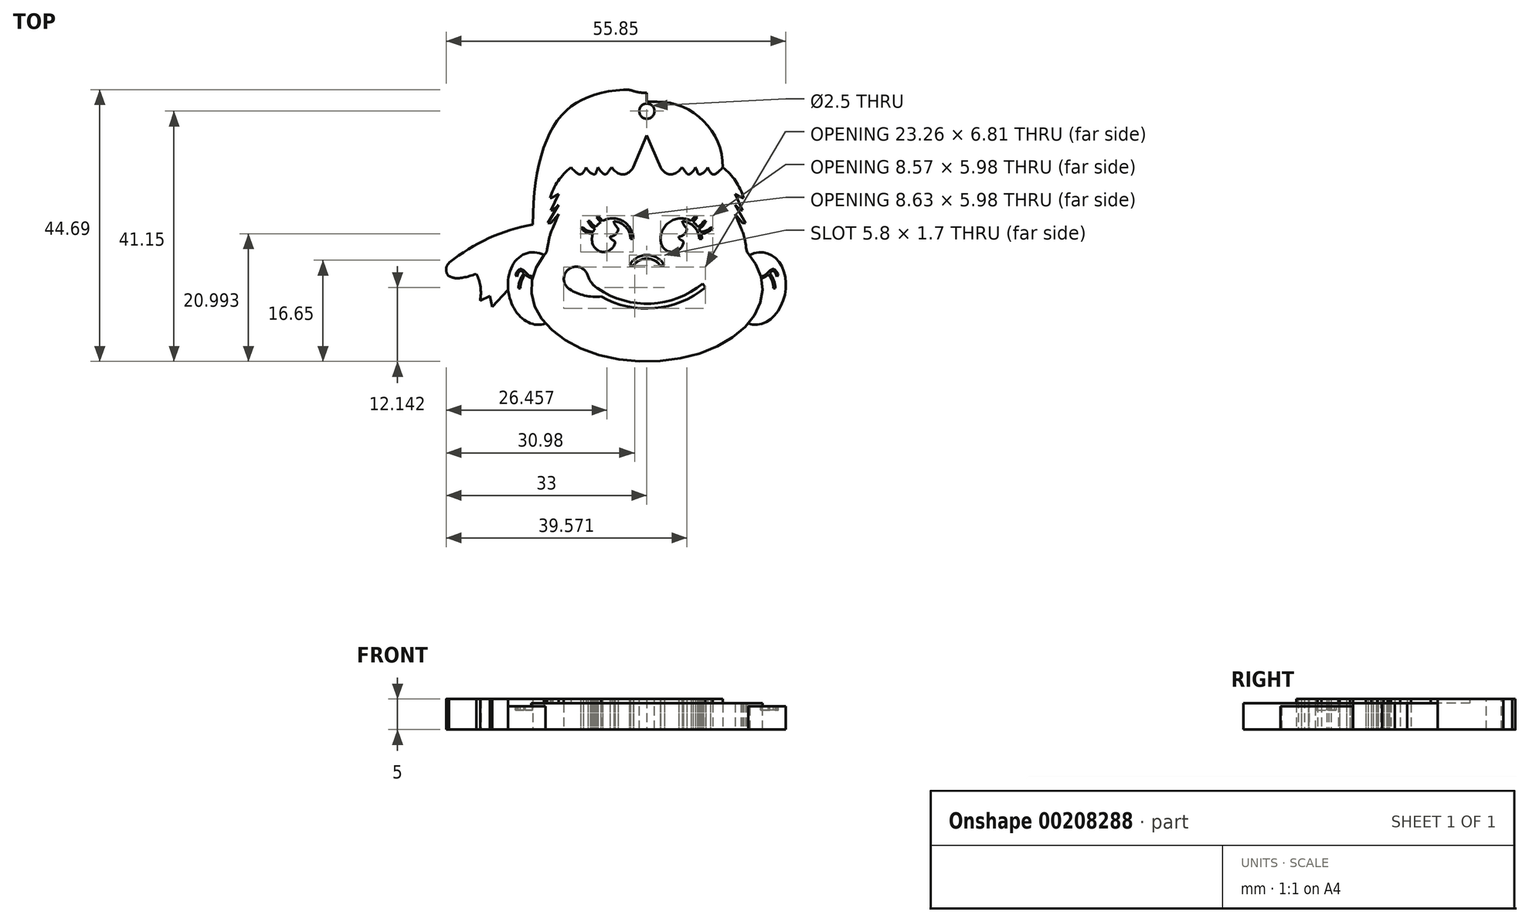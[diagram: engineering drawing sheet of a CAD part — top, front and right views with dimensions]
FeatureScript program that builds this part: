
annotation { "Feature Type Name" : "Feature", "Feature Type Description" : "" }
export const myFeature = defineFeature(function(context is Context, id is Id, definition is map)
    precondition{}
    {
        {
            var Q0;
            Q0=qCreatedBy(makeId("Top.planeOp"),FACE);
            var sketch = newSketch(context, id + "F0", { "sketchPlane" : qUnion([Q0])});
            skEllipticalArc(sketch, "E0", {});
            skLineSegment(sketch, "E1", {"start": v(-16.45, 0) * mm, "end": v(16.45, 0) * mm, "construction": true});
            skLineSegment(sketch, "E2", {"start": v(-35.38, -6) * mm, "end": v(38.73, -6) * mm, "construction": true});
            skPoint(sketch, "E2.endSnap0", {"position": v(19, -6) * mm});
            skLineSegment(sketch, "E3", {"start": v(-21.52, 12.24) * mm, "end": v(-13.55, -32.91) * mm, "construction": true});
            skEllipticalArc(sketch, "E4", {});
            skLineSegment(sketch, "E5", {"start": v(-19.34, -0.1) * mm, "end": v(-17.26, -11.9) * mm, "construction": true});
            skLineSegment(sketch, "E6", {"start": v(0, 48.23) * mm, "end": v(0, -36.68) * mm, "construction": true});
            skArc(sketch, "E7", {"start": v(2.9, -2.2) * mm, "mid": v(0, -0.5) * mm, "end": v(-2.9, -2.2) * mm});
            skLineSegment(sketch, "E8", {"start": v(-2.28, -0.5) * mm, "end": v(3.74, -0.5) * mm, "construction": true});
            skFitSpline(sketch, "E9", {"points": [v(-16.45, 0) * mm, v(-16, 2.5) * mm, v(-14.5, 6.25) * mm], "startDerivative": vector(1.72, 10.17) * mm, "endDerivative": vector(6.18, 14.8) * mm});
            skLineSegment(sketch, "E10", {"start": v(-16.25, 4.75) * mm, "end": v(-14.5, 7.75) * mm});
            skLineSegment(sketch, "E11", {"start": v(-14.5, 7.75) * mm, "end": v(-15.45, 6.85) * mm});
            skLineSegment(sketch, "E12", {"start": v(-15.45, 6.85) * mm, "end": v(-15.75, 6.85) * mm});
            skLineSegment(sketch, "E13", {"start": v(-15.75, 6.85) * mm, "end": v(-14.5, 9.5) * mm});
            skLineSegment(sketch, "E14", {"start": v(-16.25, 4.75) * mm, "end": v(-15.75, 4.75) * mm});
            skLineSegment(sketch, "E15", {"start": v(-15.75, 4.75) * mm, "end": v(-14.5, 6.25) * mm});
            skLineSegment(sketch, "E16", {"start": v(-14.5, 9.5) * mm, "end": v(-15.7, 8.9) * mm});
            skLineSegment(sketch, "E17", {"start": v(-15.7, 8.9) * mm, "end": v(-15.9, 8.9) * mm});
            skArc(sketch, "E18", {"start": v(-12.5, 13.9) * mm, "mid": v(-14.59, 11.66) * mm, "end": v(-15.9, 8.9) * mm});
            skEllipticalArc(sketch, "E19.trimOffspring", {});
            skLineSegment(sketch, "E20", {"start": v(-12.5, 13.9) * mm, "end": v(0, 13.9) * mm, "construction": true});
            skArc(sketch, "E21.MirrorCS", {"start": v(12.5, 13.9) * mm, "mid": v(14.59, 11.66) * mm, "end": v(15.9, 8.9) * mm});
            skLineSegment(sketch, "E22.MirrorCS", {"start": v(15.7, 8.9) * mm, "end": v(15.9, 8.9) * mm});
            skLineSegment(sketch, "E23.MirrorCS", {"start": v(14.5, 9.5) * mm, "end": v(15.7, 8.9) * mm});
            skLineSegment(sketch, "E24.MirrorCS", {"start": v(12.5, 13.9) * mm, "end": v(0, 13.9) * mm, "construction": true});
            skLineSegment(sketch, "E25.MirrorCS", {"start": v(15.75, 6.85) * mm, "end": v(14.5, 9.5) * mm});
            skLineSegment(sketch, "E26.MirrorCS", {"start": v(15.45, 6.85) * mm, "end": v(15.75, 6.85) * mm});
            skLineSegment(sketch, "E27.MirrorCS", {"start": v(14.5, 7.75) * mm, "end": v(15.45, 6.85) * mm});
            skLineSegment(sketch, "E28.MirrorCS", {"start": v(16.25, 4.75) * mm, "end": v(14.5, 7.75) * mm});
            skLineSegment(sketch, "E29.MirrorCS", {"start": v(16.25, 4.75) * mm, "end": v(15.75, 4.75) * mm});
            skLineSegment(sketch, "E30.MirrorCS", {"start": v(15.75, 4.75) * mm, "end": v(14.5, 6.25) * mm});
            skFitSpline(sketch, "E31.MirrorCS", {"points": [v(16.45, 0) * mm, v(16, 2.5) * mm, v(14.5, 6.25) * mm], "startDerivative": vector(-1.72, 10.17) * mm, "endDerivative": vector(-6.18, 14.8) * mm});
            skEllipticalArc(sketch, "E32.trimOffspring", {});
            skLineSegment(sketch, "E33", {"start": v(-2.9, -2.2) * mm, "end": v(-2.2, -2.2) * mm});
            skLineSegment(sketch, "E34", {"start": v(2.9, -2.2) * mm, "end": v(2.2, -2.2) * mm});
            skLineSegment(sketch, "E35", {"start": v(0, 19.2) * mm, "end": v(-2.25, 13.9) * mm});
            skEllipticalArc(sketch, "E36.MirrorCS", {});
            skLineSegment(sketch, "E37.MirrorCS", {"start": v(21.52, 12.24) * mm, "end": v(13.55, -32.91) * mm, "construction": true});
            skLineSegment(sketch, "E38", {"start": v(0, 24.7) * mm, "end": v(-1.7, 24.7) * mm});
            skArc(sketch, "E39", {"start": v(-1.7, 24.7) * mm, "mid": v(-9.34, 21.54) * mm, "end": v(-12.5, 13.9) * mm});
            skFitSpline(sketch, "E40", {"points": [v(0, 24.7) * mm, v(-8.6, 19.92) * mm, v(-10, 13.9) * mm], "startDerivative": vector(-29.01, -7.2) * mm, "endDerivative": vector(7.13, -17.68) * mm});
            skLineSegment(sketch, "E41", {"start": v(0, 13.9) * mm, "end": v(-8.6, 19.92) * mm, "construction": true});
            skLineSegment(sketch, "E42", {"start": v(-2.25, 13.9) * mm, "end": v(-2.25, 12.75) * mm, "construction": true});
            skLineSegment(sketch, "E43", {"start": v(-2.25, 12.75) * mm, "end": v(-5.75, 12.75) * mm, "construction": true});
            skLineSegment(sketch, "E44", {"start": v(-5.75, 12.75) * mm, "end": v(-5.75, 13.9) * mm, "construction": true});
            skFitSpline(sketch, "E45", {"points": [v(0, 22.2) * mm, v(-6.25, 15.4) * mm, v(-3.95, 12.75) * mm, v(-2.25, 13.9) * mm], "startDerivative": vector(-21.83, -9.77) * mm, "endDerivative": vector(2.48, 5.84) * mm});
            skLineSegment(sketch, "E46", {"start": v(-5.75, 12.75) * mm, "end": v(-22.47, 12.75) * mm, "construction": true});
            skFitSpline(sketch, "E47", {"points": [v(-10, 13.9) * mm, v(-8.7, 12.75) * mm, v(-8, 13.9) * mm], "startDerivative": vector(1.16, -2.87) * mm, "endDerivative": vector(1.96, 4.18) * mm});
            skLineSegment(sketch, "E48", {"start": v(0, 23.3) * mm, "end": v(20, 23.3) * mm, "construction": true});
            skLineSegment(sketch, "E49", {"start": v(-8.6, 16.55) * mm, "end": v(-9.48, 16.55) * mm, "construction": true});
            skFitSpline(sketch, "E50", {"points": [v(0, 23.3) * mm, v(-8.6, 16.55) * mm, v(-6.85, 12.75) * mm, v(-5.75, 13.9) * mm], "startDerivative": vector(-25.25, -9.56) * mm, "endDerivative": vector(8.03, 6.02) * mm});
            skFitSpline(sketch, "E51", {"points": [v(-12.5, 13.9) * mm, v(-10.9, 12.75) * mm, v(-10, 13.9) * mm], "startDerivative": vector(3.54, -3.37) * mm, "endDerivative": vector(1.39, 3.6) * mm});
            skLineSegment(sketch, "E52", {"start": v(0, 24.7) * mm, "end": v(0, 19.2) * mm});
            skFitSpline(sketch, "E53.MirrorCS", {"points": [v(12.5, 13.9) * mm, v(10.9, 12.75) * mm, v(10, 13.9) * mm], "startDerivative": vector(-3.54, -3.37) * mm, "endDerivative": vector(-1.39, 3.6) * mm});
            skFitSpline(sketch, "E54.MirrorCS", {"points": [v(10, 13.9) * mm, v(8.7, 12.75) * mm, v(8, 13.9) * mm], "startDerivative": vector(-1.16, -2.87) * mm, "endDerivative": vector(-1.96, 4.18) * mm});
            skFitSpline(sketch, "E55.MirrorCS", {"points": [v(0, 23.3) * mm, v(8.6, 16.55) * mm, v(6.85, 12.75) * mm, v(5.75, 13.9) * mm], "startDerivative": vector(25.25, -9.56) * mm, "endDerivative": vector(-8.03, 6.02) * mm});
            skFitSpline(sketch, "E56.MirrorCS", {"points": [v(0, 22.2) * mm, v(6.25, 15.4) * mm, v(3.95, 12.75) * mm, v(2.25, 13.9) * mm], "startDerivative": vector(21.83, -9.77) * mm, "endDerivative": vector(-2.48, 5.84) * mm});
            skLineSegment(sketch, "E57.MirrorCS", {"start": v(0, 19.2) * mm, "end": v(2.25, 13.9) * mm});
            skFitSpline(sketch, "E58.MirrorCS", {"points": [v(0, 24.7) * mm, v(8.6, 19.92) * mm, v(10, 13.9) * mm], "startDerivative": vector(29.01, -7.2) * mm, "endDerivative": vector(-7.13, -17.68) * mm});
            skArc(sketch, "E59.MirrorCS", {"start": v(1.7, 24.7) * mm, "mid": v(9.34, 21.54) * mm, "end": v(12.5, 13.9) * mm});
            skLineSegment(sketch, "E60.MirrorCS", {"start": v(0, 24.7) * mm, "end": v(1.7, 24.7) * mm});
            skEllipticalArc(sketch, "E61", {});
            skEllipticalArc(sketch, "E62.trimOffspring", {});
            skArc(sketch, "E63", {"start": v(-8.98, 1.61) * mm, "mid": v(-7.2, 0) * mm, "end": v(-5.26, 1.43) * mm});
            skArc(sketch, "E64", {"start": v(-2.25, 2.5) * mm, "mid": v(-4.06, 5.14) * mm, "end": v(-7.26, 5.1) * mm});
            skLineSegment(sketch, "E65", {"start": v(-5.5, 5.5) * mm, "end": v(-5.5, -1.83) * mm, "construction": true});
            skArc(sketch, "E66", {"start": v(-5.45, 5.07) * mm, "mid": v(-5.23, 4.5) * mm, "end": v(-4.85, 4.02) * mm});
            skArc(sketch, "E67", {"start": v(-6.04, 2.51) * mm, "mid": v(-5.88, 2.14) * mm, "end": v(-5.54, 1.91) * mm});
            skArc(sketch, "E68", {"start": v(-6.04, 2.51) * mm, "mid": v(-5.18, 2.85) * mm, "end": v(-4.72, 3.65) * mm});
            skPoint(sketch, "E69.visualSharp", {"position": v(-4.7, 3.9) * mm});
            skArc(sketch, "E69.filletArc", {"start": v(-4.72, 3.65) * mm, "mid": v(-4.74, 3.85) * mm, "end": v(-4.85, 4.02) * mm});
            skPoint(sketch, "E70.visualSharp", {"position": v(-5.2, 1.9) * mm});
            skArc(sketch, "E70.filletArc", {"start": v(-5.26, 1.43) * mm, "mid": v(-5.3, 1.73) * mm, "end": v(-5.54, 1.91) * mm});
            skPoint(sketch, "E71.start.orphan", {"position": v(-8.75, 2.5) * mm});
            skLineSegment(sketch, "E72", {"start": v(-7.26, 5.1) * mm, "end": v(-8, 5.98) * mm});
            skLineSegment(sketch, "E73", {"start": v(-8, 5.98) * mm, "end": v(-8.3, 5.73) * mm});
            skLineSegment(sketch, "E74", {"start": v(-8.3, 5.73) * mm, "end": v(-7.6, 4.89) * mm});
            skArc(sketch, "E75.trimOffspring", {"start": v(-7.6, 4.89) * mm, "mid": v(-8.01, 4.54) * mm, "end": v(-8.36, 4.14) * mm});
            skArc(sketch, "E76", {"start": v(-9.3, 5.05) * mm, "mid": v(-8.91, 4.51) * mm, "end": v(-8.36, 4.14) * mm});
            skArc(sketch, "E77", {"start": v(-9.7, 5.05) * mm, "mid": v(-9.25, 4.34) * mm, "end": v(-8.56, 3.83) * mm});
            skLineSegment(sketch, "E78", {"start": v(-9.7, 5.05) * mm, "end": v(-9.3, 5.05) * mm});
            skArc(sketch, "E79.trimOffspring", {"start": v(-8.56, 3.83) * mm, "mid": v(-8.7, 3.58) * mm, "end": v(-8.8, 3.33) * mm});
            skArc(sketch, "E80", {"start": v(-10.46, 4) * mm, "mid": v(-9.7, 3.47) * mm, "end": v(-8.8, 3.33) * mm});
            skLineSegment(sketch, "E81", {"start": v(-10.46, 4) * mm, "end": v(-10.86, 4) * mm});
            skArc(sketch, "E82", {"start": v(-10.86, 4) * mm, "mid": v(-10, 3.26) * mm, "end": v(-8.9, 3) * mm});
            skArc(sketch, "E83.trimOffspring", {"start": v(-8.9, 3) * mm, "mid": v(-9.02, 2.31) * mm, "end": v(-8.98, 1.61) * mm});
            skLineSegment(sketch, "E84", {"start": v(0, 54) * mm, "end": v(50, 54) * mm, "construction": true});
            skLineSegment(sketch, "E85", {"start": v(50, 54) * mm, "end": v(50, -14.33) * mm, "construction": true});
            skLineSegment(sketch, "E86", {"start": v(55.52, 54) * mm, "end": v(55.52, -14.1) * mm, "construction": true});
            skArc(sketch, "E87", {"start": v(-8.1, -6) * mm, "mid": v(0, -8.5) * mm, "end": v(8.1, -6) * mm, "construction": true});
            skArc(sketch, "E88", {"start": v(-8.1, -6) * mm, "mid": v(0.67, -8.48) * mm, "end": v(9.16, -5.2) * mm});
            skLineSegment(sketch, "E89", {"start": v(9.16, -5.2) * mm, "end": v(9.61, -5.86) * mm});
            skLineSegment(sketch, "E90", {"start": v(-10.95, -7.1) * mm, "end": v(9.68, -7.1) * mm, "construction": true});
            skArc(sketch, "E91", {"start": v(-9.75, -3.8) * mm, "mid": v(-9.1, -5.04) * mm, "end": v(-8.1, -6) * mm});
            skArc(sketch, "E92", {"start": v(-9.75, -3.8) * mm, "mid": v(-12.88, -2.84) * mm, "end": v(-12.73, -6.1) * mm});
            skArc(sketch, "E93", {"start": v(-12.73, -6.1) * mm, "mid": v(-10.22, -7.16) * mm, "end": v(-7.5, -7.31) * mm});
            skArc(sketch, "E94", {"start": v(-7.5, -7.31) * mm, "mid": v(1.28, -9.24) * mm, "end": v(9.61, -5.86) * mm});
            skArc(sketch, "E95", {"start": v(-2.23, 2.13) * mm, "mid": v(-2.23, 2.31) * mm, "end": v(-2.25, 2.5) * mm});
            skLineSegment(sketch, "E96", {"start": v(-2.68, 2.13) * mm, "end": v(-2.23, 2.13) * mm});
            skArc(sketch, "E97", {"start": v(2.2, -2.2) * mm, "mid": v(0, -1.09) * mm, "end": v(-2.2, -2.2) * mm});
            skLineSegment(sketch, "E98", {"start": v(-18.75, 27.8) * mm, "end": v(-18.75, -30.49) * mm, "construction": true});
            skLineSegment(sketch, "E99", {"start": v(-15.9, 26.75) * mm, "end": v(30.98, 26.75) * mm, "construction": true});
            skLineSegment(sketch, "E100", {"start": v(-34.8, 4.5) * mm, "end": v(31.88, 4.5) * mm, "construction": true});
            skFitSpline(sketch, "E101", {"points": [v(-18.75, 4.5) * mm, v(-13.75, 22.75) * mm, v(-2.5, 26.75) * mm], "startDerivative": vector(0, 44.41) * mm, "endDerivative": vector(32.74, 1.2) * mm});
            skEllipticalArc(sketch, "E102", {});
            skArc(sketch, "E103.filletArc", {"start": v(-2.11, 26.43) * mm, "mid": v(-2.95, 26.65) * mm, "end": v(-3.82, 26.68) * mm});
            skLineSegment(sketch, "E104", {"start": v(-33, 13.01) * mm, "end": v(-33, -15.44) * mm, "construction": true});
            skLineSegment(sketch, "E105", {"start": v(-45.55, -3.5) * mm, "end": v(13.92, -3.5) * mm, "construction": true});
            skArc(sketch, "E106", {"start": v(-18.75, 4.5) * mm, "mid": v(-26, 2.25) * mm, "end": v(-32.44, -1.74) * mm});
            skArc(sketch, "E107", {"start": v(-32.44, -1.74) * mm, "mid": v(-33, -2.84) * mm, "end": v(-32.55, -3.98) * mm});
            skArc(sketch, "E108", {"start": v(-27.41, -8) * mm, "mid": v(-27.35, -5.76) * mm, "end": v(-28.02, -3.62) * mm});
            skLineSegment(sketch, "E109", {"start": v(-27.41, -8) * mm, "end": v(-25.81, -7.21) * mm});
            skLineSegment(sketch, "E110", {"start": v(-25.81, -7.21) * mm, "end": v(-25.41, -9) * mm});
            skLineSegment(sketch, "E111", {"start": v(-25.41, -9) * mm, "end": v(-22.81, -6.2) * mm});
            skFitSpline(sketch, "E112", {"points": [v(-32.55, -3.98) * mm, v(-30.97, -4.3) * mm, v(-24.48, -2.33) * mm], "startDerivative": vector(4.01, -1.65) * mm, "endDerivative": vector(11.28, 4.26) * mm});
            skPoint(sketch, "E113.orphan", {"position": v(-28.21, -3.27) * mm});
            skLineSegment(sketch, "E114", {"start": v(0, 26.15) * mm, "end": v(0, 24.7) * mm});
            skArc(sketch, "E115.1.0.0", {"start": v(2.38, 3) * mm, "mid": v(2.26, 2.31) * mm, "end": v(2.3, 1.61) * mm});
            skArc(sketch, "E115.1.0.1", {"start": v(2.3, 1.61) * mm, "mid": v(4.09, 0) * mm, "end": v(6.02, 1.43) * mm});
            skArc(sketch, "E115.1.0.2", {"start": v(6.02, 1.43) * mm, "mid": v(5.98, 1.73) * mm, "end": v(5.74, 1.91) * mm});
            skArc(sketch, "E115.1.0.3", {"start": v(5.24, 2.51) * mm, "mid": v(5.4, 2.14) * mm, "end": v(5.74, 1.91) * mm});
            skArc(sketch, "E115.1.0.4", {"start": v(5.24, 2.51) * mm, "mid": v(6.1, 2.85) * mm, "end": v(6.56, 3.65) * mm});
            skArc(sketch, "E115.1.0.5", {"start": v(6.56, 3.65) * mm, "mid": v(6.54, 3.85) * mm, "end": v(6.43, 4.02) * mm});
            skArc(sketch, "E115.1.0.6", {"start": v(5.83, 5.07) * mm, "mid": v(6.05, 4.5) * mm, "end": v(6.43, 4.02) * mm});
            skLineSegment(sketch, "E115.1.0.9", {"start": v(8.6, 2.13) * mm, "end": v(9.05, 2.13) * mm});
            skLineSegment(sketch, "E115.direction1", {"start": v(-8.98, 1.61) * mm, "end": v(2.3, 1.61) * mm, "construction": true});
            skArc(sketch, "E116", {"start": v(9.05, 2.13) * mm, "mid": v(9.02, 2.57) * mm, "end": v(8.93, 3) * mm});
            skArc(sketch, "E117.MirrorCS", {"start": v(10.86, 4) * mm, "mid": v(10.02, 3.27) * mm, "end": v(8.93, 3) * mm});
            skLineSegment(sketch, "E118.MirrorCS", {"start": v(9.7, 5.05) * mm, "end": v(9.3, 5.05) * mm});
            skArc(sketch, "E119.MirrorCS", {"start": v(9.7, 5.05) * mm, "mid": v(9.25, 4.35) * mm, "end": v(8.59, 3.84) * mm});
            skLineSegment(sketch, "E120.MirrorCS", {"start": v(10.46, 4) * mm, "end": v(10.86, 4) * mm});
            skArc(sketch, "E121.MirrorCS", {"start": v(10.46, 4) * mm, "mid": v(9.72, 3.48) * mm, "end": v(8.83, 3.33) * mm});
            skArc(sketch, "E122.MirrorCS", {"start": v(9.3, 5.05) * mm, "mid": v(8.92, 4.52) * mm, "end": v(8.38, 4.15) * mm});
            skLineSegment(sketch, "E123.MirrorCS", {"start": v(7.27, 5.11) * mm, "end": v(8, 5.98) * mm});
            skLineSegment(sketch, "E124.MirrorCS", {"start": v(8, 5.98) * mm, "end": v(8.3, 5.73) * mm});
            skLineSegment(sketch, "E125.MirrorCS", {"start": v(8.3, 5.73) * mm, "end": v(7.61, 4.9) * mm});
            skPoint(sketch, "E126.orphan", {"position": v(7.26, 5.1) * mm});
            skPoint(sketch, "E127.orphan", {"position": v(7.6, 4.89) * mm});
            skArc(sketch, "E128.trimOffspring", {"start": v(7.27, 5.11) * mm, "mid": v(4.31, 5.25) * mm, "end": v(2.38, 3) * mm});
            skPoint(sketch, "E129.orphan", {"position": v(8.9, 3) * mm});
            skPoint(sketch, "E130.orphan", {"position": v(8.8, 3.33) * mm});
            skArc(sketch, "E131.trimOffspring", {"start": v(8.83, 3.33) * mm, "mid": v(8.72, 3.59) * mm, "end": v(8.59, 3.84) * mm});
            skArc(sketch, "E132.trimOffspring", {"start": v(8.38, 4.15) * mm, "mid": v(8.03, 4.56) * mm, "end": v(7.61, 4.9) * mm});
            skPoint(sketch, "E133.orphan", {"position": v(8.36, 4.14) * mm});
            skPoint(sketch, "E134.orphan", {"position": v(8.56, 3.83) * mm});
            skArc(sketch, "E135", {"start": v(-2.68, 2.13) * mm, "mid": v(-3.48, 4.15) * mm, "end": v(-5.45, 5.07) * mm});
            skPoint(sketch, "E136.orphan", {"position": v(-5.47, 5.17) * mm});
            skArc(sketch, "E137", {"start": v(8.6, 2.13) * mm, "mid": v(7.8, 4.15) * mm, "end": v(5.83, 5.07) * mm});
            skPoint(sketch, "E138.orphan", {"position": v(5.8, 5.17) * mm});
            const initialGuessF0  = {"E0": [0, -0.006, 1, 0, 0.019, 0.012, 2.6179938779914944, 2.668435409031319], "E4": [-0.0183, -0.006, -0.17364817766693047, 0.9848077530122081, 0.006, 0.0045, 5.742579078983642, 3.2755769125221526], "E19.trimOffspring": [0, -0.006, 1, 0, 0.019, 0.012, 3.641440500266903, 5.7833374605024765], "E32.trimOffspring": [0, -0.006, 1, 0, 0.019, 0.012, 0.47315724455847397, 0.5235987755982988], "E36.MirrorCS": [0.0183, -0.006, 0.17364817766693047, 0.9848077530122081, 0.006, 0.0045, 3.0076083946574337, 0.5406062281959443], "E61": [0, -0.006, 1, 0, 0.019, 0.012, 2.6684354090313196, 3.6414405002669024], "E62.trimOffspring": [0, -0.006, 1, 0, 0.019, 0.012, 5.7833374605024765, 0.47315724455847347], "E102": [0, 0.02675, -1, 0, 0.0025, 0.0006, 0.5643852426448737, 1.5707963267948966]};
            skSetInitialGuess(sketch, initialGuessF0);
            skSolve(sketch);
        }
        {
            var Q0;
            Q0=makeQuery(id+"F0.imprint","IMPRINT",FACE,{"disambiguationData":[TD([[makeQuery(id+"F0.imprint","IMPRINT",EDGE,{"derivedFrom":sQuery(id+"F0.wireOp",EDGE,"E0")}),1.0]])]});
            var Q1;
            Q1=makeQuery(id+"F0.imprint","IMPRINT",FACE,{"disambiguationData":[TD([[makeQuery(id+"F0.imprint","IMPRINT",EDGE,{"derivedFrom":sQuery(id+"F0.wireOp",EDGE,"ICi0ZoLA-6eNF-tacr-hD6t-iQozf2GyN9Os")}),1.0]])]});
            var Q2;
            Q2=makeQuery(id+"F0.imprint","IMPRINT",FACE,{"disambiguationData":[TD([[makeQuery(id+"F0.imprint","IMPRINT",EDGE,{"derivedFrom":sQuery(id+"F0.wireOp",EDGE,"Alc9XebQ-BCgD-IBuf-yUf6-nh8GaAThc2JX")}),-1.0]])]});
            var Q3;
            Q3=makeQuery(id+"F0.imprint","IMPRINT",FACE,{"disambiguationData":[TD([[makeQuery(id+"F0.imprint","IMPRINT",EDGE,{"derivedFrom":sQuery(id+"F0.wireOp",EDGE,"39c14105-0e34-43a8-b0d7-4433907fe2a90.MirrorCS")}),1.0]])]});
            extrude(context, id + "F1", {"entities" : qUnion([Q0, Q1, Q2, Q3]), "depth" : 4.3 * mm});
        }
        {
            var Q0;
            Q0=makeQuery(id+"F0.imprint","IMPRINT",FACE,{"disambiguationData":[TD([[makeQuery(id+"F0.imprint","IMPRINT",EDGE,{"derivedFrom":sQuery(id+"F0.wireOp",EDGE,"E38")}),1.0]])]});
            var Q1;
            {var subQ0=sQuery(id+"F0.wireOp",EDGE,"E40");Q1=makeQuery(id+"F0.imprint","IMPRINT",FACE,{"disambiguationData":[TD([[makeQuery(id+"F0.imprint","IMPRINT",EDGE,{"derivedFrom":subQ0}),1.0]])]});}
            var Q2;
            {var subQ3=sQuery(id+"F0.wireOp",EDGE,"E50");var subQ5=makeQuery(id+"F0.imprint","INTERSECT",VERTEX,{"derivedFrom":[sQuery(id+"F0.wireOp",EDGE,"E47"),subQ3]});Q2=makeQuery(id+"F0.imprint","IMPRINT",FACE,{"disambiguationData":[TD([[makeQuery(id+"F0.imprint","IMPRINT",EDGE,{"disambiguationData":[TD([[subQ5,-1.0]])],"derivedFrom":subQ3}),1.0]])]});}
            var Q3;
            {var subQ0=sQuery(id+"F0.wireOp",EDGE,"E35");Q3=makeQuery(id+"F0.imprint","IMPRINT",FACE,{"disambiguationData":[TD([[makeQuery(id+"F0.imprint","IMPRINT",EDGE,{"derivedFrom":subQ0}),-1.0]])]});}
            var Q4;
            {var subQ0=sQuery(id+"F0.wireOp",EDGE,"E57.MirrorCS");Q4=makeQuery(id+"F0.imprint","IMPRINT",FACE,{"disambiguationData":[TD([[makeQuery(id+"F0.imprint","IMPRINT",EDGE,{"derivedFrom":subQ0}),1.0]])]});}
            var Q5;
            {var subQ3=sQuery(id+"F0.wireOp",EDGE,"E55.MirrorCS");var subQ5=makeQuery(id+"F0.imprint","INTERSECT",VERTEX,{"derivedFrom":[sQuery(id+"F0.wireOp",EDGE,"E54.MirrorCS"),subQ3]});Q5=makeQuery(id+"F0.imprint","IMPRINT",FACE,{"disambiguationData":[TD([[makeQuery(id+"F0.imprint","IMPRINT",EDGE,{"disambiguationData":[TD([[subQ5,-1.0]])],"derivedFrom":subQ3}),-1.0]])]});}
            var Q6;
            {var subQ4=sQuery(id+"F0.wireOp",EDGE,"E54.MirrorCS");Q6=makeQuery(id+"F0.imprint","IMPRINT",FACE,{"disambiguationData":[TD([[makeQuery(id+"F0.imprint","IMPRINT",EDGE,{"derivedFrom":subQ4}),-1.0]])]});}
            var Q7;
            Q7=makeQuery(id+"F0.imprint","IMPRINT",FACE,{"disambiguationData":[TD([[makeQuery(id+"F0.imprint","IMPRINT",EDGE,{"derivedFrom":sQuery(id+"F0.wireOp",EDGE,"E53.MirrorCS")}),-1.0]])]});
            extrude(context, id + "F2", {"entities" : qUnion([Q0, Q1, Q2, Q3, Q4, Q5, Q6, Q7]), "depth" : 5 * mm});
        }
        {
            var Q0;
            Q0=makeQuery(id+"F0.imprint","IMPRINT",FACE,{"disambiguationData":[TD([[makeQuery(id+"F0.imprint","IMPRINT",EDGE,{"derivedFrom":sQuery(id+"F0.wireOp",EDGE,"E4")}),1.0]])]});
            var Q1;
            Q1=makeQuery(id+"F0.imprint","IMPRINT",FACE,{"disambiguationData":[TD([[makeQuery(id+"F0.imprint","IMPRINT",EDGE,{"derivedFrom":sQuery(id+"F0.wireOp",EDGE,"E36.MirrorCS")}),1.0]])]});
            extrude(context, id + "F3", {"entities" : qUnion([Q0, Q1]), "depth" : 3.8 * mm});
        }
        {
            var Q0;
            Q0=makeQuery(id+"F0.imprint","IMPRINT",FACE,{"disambiguationData":[TD([[makeQuery(id+"F0.imprint","IMPRINT",EDGE,{"derivedFrom":sQuery(id+"F0.wireOp",EDGE,"E63")}),1.0]])]});
            var Q1;
            Q1=makeQuery(id+"F0.imprint","IMPRINT",FACE,{"disambiguationData":[TD([[makeQuery(id+"F0.imprint","IMPRINT",EDGE,{"derivedFrom":sQuery(id+"F0.wireOp",EDGE,"E115.1.0.0")}),1.0]])]});
            extrude(context, id + "F4", {"entities" : qUnion([Q0, Q1]), "depth" : 5 * mm});
        }
        {
            var Q0;
            Q0=makeQuery(id+"F0.imprint","IMPRINT",FACE,{"disambiguationData":[TD([[makeQuery(id+"F0.imprint","IMPRINT",EDGE,{"derivedFrom":sQuery(id+"F0.wireOp",EDGE,"E88")}),-1.0]])]});
            extrude(context, id + "F5", {"entities" : qUnion([Q0]), "depth" : 5 * mm});
        }
        {
            var Q0;
            Q0=makeQuery(id+"F3.opExtrude","CAP_FACE",FACE,{"disambiguationData":[OSD([sQuery(id+"F0.wireOp",EDGE,"E4"),sQuery(id+"F0.wireOp",EDGE,"E61")])],"isStart":false});
            var sketch = newSketch(context, id + "F6", { "sketchPlane" : qUnion([Q0])});
            skFitSpline(sketch, "E139", {"points": [v(-18.73, -4) * mm, v(-19.78, -3.5) * mm, v(-20.75, -2.8) * mm, v(-21.65, -3.65) * mm], "startDerivative": vector(-4.75, 0) * mm, "endDerivative": vector(-3.24, -3.98) * mm});
            skArc(sketch, "E140", {"start": v(-19.98, -3.72) * mm, "mid": v(-20.6, -4.79) * mm, "end": v(-20.8, -6) * mm});
            skArc(sketch, "E141", {"start": v(-20.2, -3.5) * mm, "mid": v(-20.87, -4.67) * mm, "end": v(-21.1, -6) * mm});
            skFitSpline(sketch, "E142", {"points": [v(-21.35, -4.05) * mm, v(-20.75, -3.1) * mm, v(-20.2, -3.5) * mm, v(-18.8, -4.3) * mm], "startDerivative": vector(0.59, 3.43) * mm, "endDerivative": vector(3.34, 0.02) * mm});
            skLineSegment(sketch, "E143", {"start": v(-21.65, -3.65) * mm, "end": v(-21.35, -4.05) * mm});
            skLineSegment(sketch, "E144", {"start": v(-21.1, -6) * mm, "end": v(-20.8, -6) * mm});
            skPoint(sketch, "E145.orphan", {"position": v(-20, -3.29) * mm});
            skLineSegment(sketch, "E146", {"start": v(-18.73, -4) * mm, "end": v(-18.8, -4.3) * mm});
            skFitSpline(sketch, "E147.MirrorCS", {"points": [v(21.35, -4.05) * mm, v(20.75, -3.1) * mm, v(20.2, -3.5) * mm, v(18.8, -4.3) * mm], "startDerivative": vector(-0.59, 3.43) * mm, "endDerivative": vector(-3.34, 0.02) * mm});
            skLineSegment(sketch, "E148.MirrorCS", {"start": v(18.73, -4) * mm, "end": v(18.8, -4.3) * mm});
            skFitSpline(sketch, "E149.MirrorCS", {"points": [v(18.73, -4) * mm, v(19.78, -3.5) * mm, v(20.75, -2.8) * mm, v(21.65, -3.65) * mm], "startDerivative": vector(4.75, 0) * mm, "endDerivative": vector(3.24, -3.98) * mm});
            skArc(sketch, "E150.MirrorCS", {"start": v(19.98, -3.72) * mm, "mid": v(20.6, -4.79) * mm, "end": v(20.8, -6) * mm});
            skArc(sketch, "E151.MirrorCS", {"start": v(20.2, -3.5) * mm, "mid": v(20.87, -4.67) * mm, "end": v(21.1, -6) * mm});
            skLineSegment(sketch, "E152.MirrorCS", {"start": v(21.1, -6) * mm, "end": v(20.8, -6) * mm});
            skLineSegment(sketch, "E153.MirrorCS", {"start": v(21.65, -3.65) * mm, "end": v(21.35, -4.05) * mm});
            skFitSpline(sketch, "E154.MirrorCS", {"points": [v(21.35, -4.05) * mm, v(20.75, -3.1) * mm, v(20.2, -3.5) * mm, v(18.8, -4.3) * mm], "startDerivative": vector(-0.59, 3.43) * mm, "endDerivative": vector(-3.34, 0.02) * mm});
            skSolve(sketch);
        }
        {
            var Q0;
            Q0 = qSketchRegion(id + "F6", true);
            extrude(context, id + "F7", {"entities" : qUnion([Q0]), "operationType" : NewBodyOperationType.REMOVE, "oppositeDirection" : true, "depth" : 0.6 * mm});
        }
        {
            var Q0;
            Q0=makeQuery(id+"F0.imprint","IMPRINT",FACE,{"disambiguationData":[TD([[makeQuery(id+"F0.imprint","IMPRINT",EDGE,{"derivedFrom":sQuery(id+"F0.wireOp",EDGE,"E7")}),1.0]])]});
            extrude(context, id + "F8", {"entities" : qUnion([Q0]), "depth" : 5 * mm});
        }
        {
            var Q0;
            {var subQ1=sQuery(id+"F0.wireOp",EDGE,"E0");Q0=makeQuery(id+"F0.imprint","IMPRINT",FACE,{"disambiguationData":[TD([[makeQuery(id+"F0.imprint","IMPRINT",EDGE,{"derivedFrom":subQ1}),-1.0]])]});}
            extrude(context, id + "F9", {"entities" : qUnion([Q0]), "operationType" : NewBodyOperationType.ADD, "depth" : 5 * mm});
        }
        {
            var Q0;
            {var subQ0=sQuery(id+"F0.wireOp",EDGE,"E114");var subQ1=sQuery(id+"F0.wireOp",EDGE,"E112");var subQ2=sQuery(id+"F0.wireOp",EDGE,"E111");var subQ3=sQuery(id+"F0.wireOp",EDGE,"E110");var subQ4=sQuery(id+"F0.wireOp",EDGE,"E109");var subQ5=sQuery(id+"F0.wireOp",EDGE,"E108");var subQ6=sQuery(id+"F0.wireOp",EDGE,"E107");var subQ7=sQuery(id+"F0.wireOp",EDGE,"E106");var subQ8=sQuery(id+"F0.wireOp",EDGE,"E103.filletArc");var subQ9=sQuery(id+"F0.wireOp",EDGE,"E102");var subQ10=sQuery(id+"F0.wireOp",EDGE,"E101");var subQ11=sQuery(id+"F0.wireOp",EDGE,"E39");var subQ12=sQuery(id+"F0.wireOp",EDGE,"E38");var subQ13=sQuery(id+"F0.wireOp",EDGE,"E18");var subQ14=sQuery(id+"F0.wireOp",EDGE,"E17");var subQ15=sQuery(id+"F0.wireOp",EDGE,"E16");var subQ16=sQuery(id+"F0.wireOp",EDGE,"E15");var subQ17=sQuery(id+"F0.wireOp",EDGE,"E14");var subQ18=sQuery(id+"F0.wireOp",EDGE,"E13");var subQ19=sQuery(id+"F0.wireOp",EDGE,"E12");var subQ20=sQuery(id+"F0.wireOp",EDGE,"E11");var subQ21=sQuery(id+"F0.wireOp",EDGE,"E10");var subQ22=sQuery(id+"F0.wireOp",EDGE,"E9");var subQ23=sQuery(id+"F0.wireOp",EDGE,"E4");var subQ24=sQuery(id+"F0.wireOp",EDGE,"E0");Q0=makeQuery(id+"FpA3KZrnlwLrEnR_1.1.F9.boolean.opBoolean","MERGE",FACE,{"derivedFrom":[makeQuery(id+"F9.boolean.opBoolean","MERGE",FACE,{"derivedFrom":[makeQuery(id+"F2.opExtrude","CAP_FACE",FACE,{"disambiguationData":[OSD([sQuery(id+"F0.wireOp",EDGE,"E35"),subQ12,subQ11,sQuery(id+"F0.wireOp",EDGE,"E45"),sQuery(id+"F0.wireOp",EDGE,"E47"),sQuery(id+"F0.wireOp",EDGE,"E50"),sQuery(id+"F0.wireOp",EDGE,"E51"),sQuery(id+"F0.wireOp",EDGE,"E53.MirrorCS"),sQuery(id+"F0.wireOp",EDGE,"E54.MirrorCS"),sQuery(id+"F0.wireOp",EDGE,"E55.MirrorCS"),sQuery(id+"F0.wireOp",EDGE,"E56.MirrorCS"),sQuery(id+"F0.wireOp",EDGE,"E57.MirrorCS"),sQuery(id+"F0.wireOp",EDGE,"E59.MirrorCS"),sQuery(id+"F0.wireOp",EDGE,"E60.MirrorCS")])],"isStart":false}),makeQuery(id+"F9.opExtrude","CAP_FACE",FACE,{"disambiguationData":[OSD([subQ24,subQ23,subQ22,subQ21,subQ20,subQ19,subQ18,subQ17,subQ16,subQ15,subQ14,subQ13,subQ12,subQ11,subQ10,subQ9,subQ8,subQ7,subQ6,subQ5,subQ4,subQ3,subQ2,subQ1,subQ0])],"isStart":false})]}),makeQuery(id+"FpA3KZrnlwLrEnR_1.1.F9.opExtrude","CAP_FACE",FACE,{"disambiguationData":[OSD([subQ24,subQ23,subQ22,subQ21,subQ20,subQ19,subQ18,subQ17,subQ16,subQ15,subQ14,subQ13,subQ12,subQ11,subQ10,subQ9,subQ8,subQ7,subQ6,subQ5,subQ4,subQ3,subQ2,subQ1,subQ0])],"isStart":false})]});}
            var sketch = newSketch(context, id + "F10", { "sketchPlane" : qUnion([Q0])});
            skCircle(sketch, "E155", {"center": v(0, 23.15) * mm, "radius": 1.25 * mm});
            skSolve(sketch);
        }
        {
            var Q0;
            Q0 = qSketchRegion(id + "F10", true);
            extrude(context, id + "F11", {"entities" : qUnion([Q0]), "operationType" : NewBodyOperationType.REMOVE, "oppositeDirection" : true, "depth" : 25 * mm});
        }
        {
            var Q0;
            Q0=makeQuery(id+"F6.imprint","IMPRINT",FACE,{"disambiguationData":[TD([[makeQuery(id+"F6.imprint","IMPRINT",EDGE,{"derivedFrom":sQuery(id+"F6.wireOp",EDGE,"E147.MirrorCS")}),-1.0]])]});
            extrude(context, id + "F12", {"entities" : qUnion([Q0]), "operationType" : NewBodyOperationType.REMOVE, "oppositeDirection" : true, "depth" : 0.4 * mm});
        }
    });
